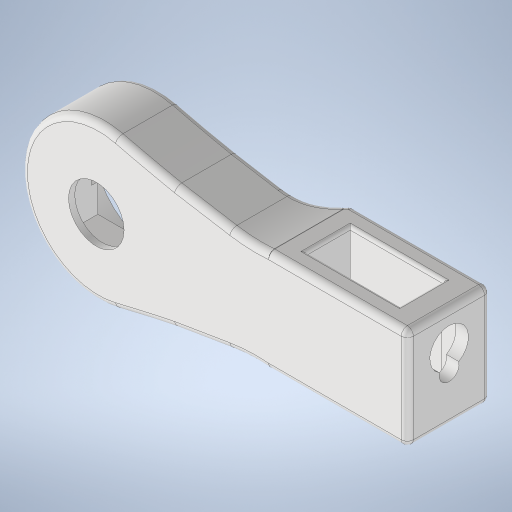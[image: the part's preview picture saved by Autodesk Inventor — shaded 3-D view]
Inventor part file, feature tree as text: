
AUTODESK INVENTOR PART (.ipt)
format: ipt  version: 2024 (Build 280153000, 153)  size: 982,528 bytes
history: native  units: mm
features: extrude x11, projected_geometry x9, plane x6, fillet x6, other x6, reference x3, mirror x2
ambient origin geometry x8: Origin, YZ Plane, XZ Plane, XY Plane, X Axis, Y Axis, Z Axis, Center Point
bodies: Solid1 (feature_tree)
feature tree (43):
  plane  "Work Plane1"
  extrude  "Extrusion1"  Depth=40.25mm
  extrude  "Extrusion2"  Depth=20.25mm
  plane  "Work Plane2"
  extrude  "Extrusion3"  TaperAngle=0.0deg  [1 undecoded]
  mirror  "Mirror2"
  extrude  "Extrusion4"  Depth=40.25mm
  extrude  "Extrusion6"  Depth=50.0mm
  fillet  "Fillet1"  Radius=55.0mm
  extrude  "Extrusion7"  Depth=15.0mm
  extrude  "Extrusion8"  Depth=15.0mm
  extrude  "Extrusion9"  Depth=20.0mm
  extrude  "Extrusion10"  Depth=20.0mm
  plane  "Work Plane3"
  fillet  "Fillet7"  Radius=12.817996mm
  fillet  "Fillet8"  Radius=12.817996mm
  fillet  "Fillet10"  Radius=8.0mm
  extrude  "Extrusion12"  Depth=10.125mm
  fillet  "Fillet15"  Radius=5.5mm
  fillet  "Fillet16"  Radius=1.0mm
  extrude  "Extrusion15"  Depth=1.0mm
  plane  "Work Plane7"
  plane  "Work Plane8"
  plane  "Work Plane9"
  mirror  "Mirror5"
  reference  "Reference1"
  reference  "Reference2"
  reference  "Reference3"
  projected_geometry  "Projected Loop1"
  projected_geometry  "Projected Loop2"
  projected_geometry  "Projected Loop3"
  projected_geometry  "Projected Loop5"
  projected_geometry  "Projected Loop7"
  projected_geometry  "Projected Loop8"
  projected_geometry  "Projected Loop10"
  projected_geometry  "Projected Loop12"
  projected_geometry  "Projected Loop14"
  other  "<userpath> windows\Documents\Inventor\Robotska_roka\Assembly4.iam"
  other  "Assembly4.iam"
  other  "Servo Motor MG996R  With Attachments:5"
  other  "servoMotorMG996R_7"
  other  "Servo Motor MG996R  With Attachments:6"
  other  "attachmentCircular_1"
note: 1 required parameter value undecoded (feature->parameter linkage not recoverable at this tier; creation-order binding heuristic only, values carry confidence <= 0.55)
